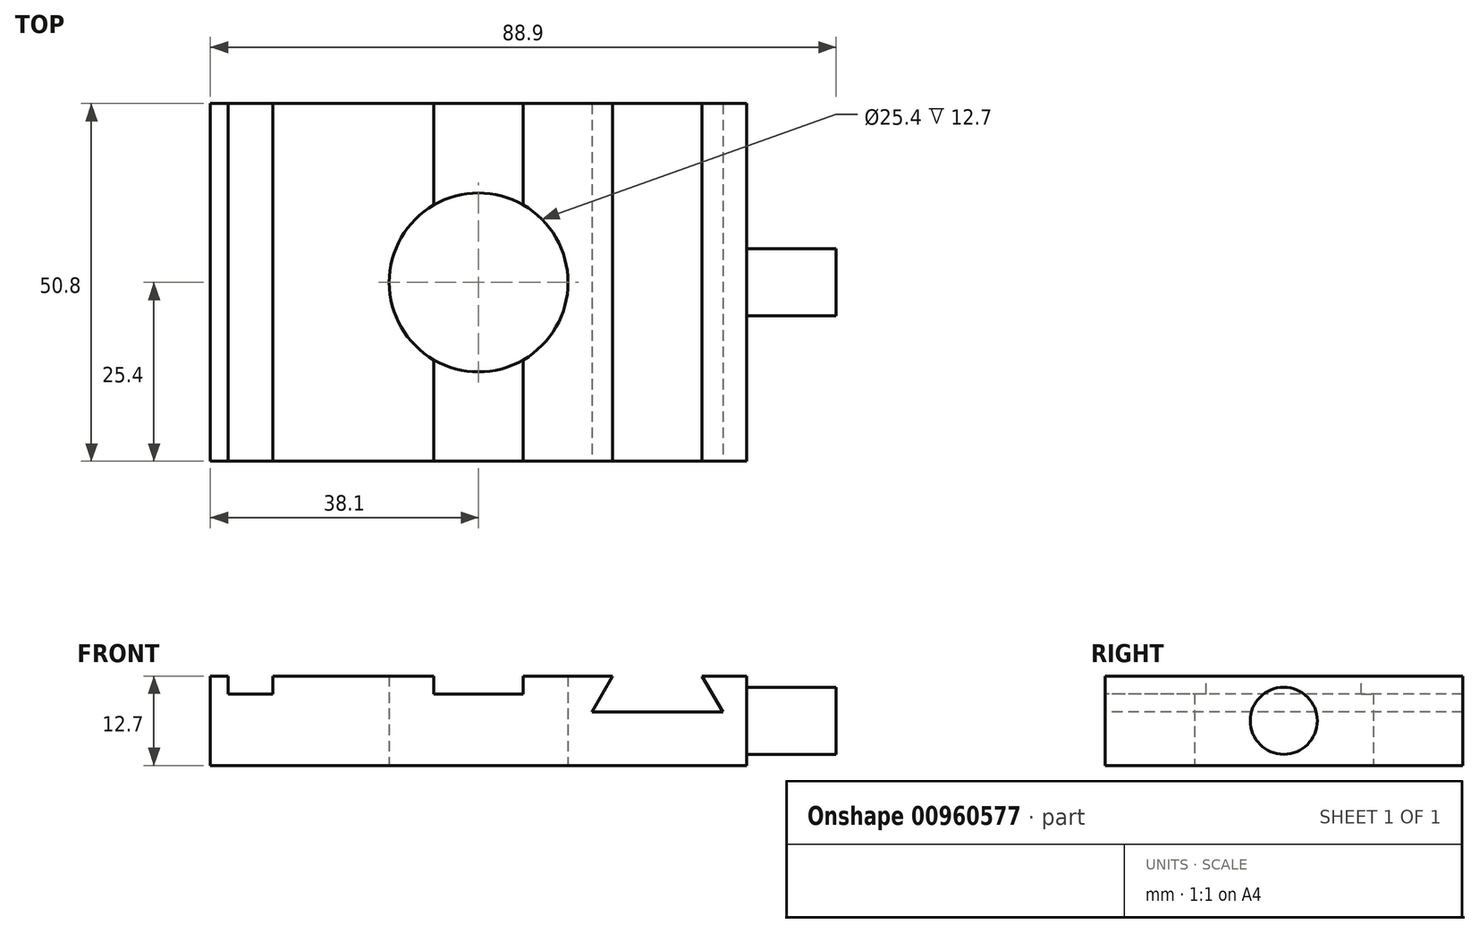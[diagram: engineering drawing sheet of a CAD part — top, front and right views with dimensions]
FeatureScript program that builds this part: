
annotation { "Feature Type Name" : "Feature", "Feature Type Description" : "" }
export const myFeature = defineFeature(function(context is Context, id is Id, definition is map)
    precondition{}
    {
        {
            var Q0;
            Q0=qCreatedBy(makeId("Top.planeOp"),FACE);
            var sketch = newSketch(context, id + "F0", { "sketchPlane" : qUnion([Q0])});
            skLineSegment(sketch, "E0.bottom", {"start": v(38.1, -25.4) * mm, "end": v(-38.1, -25.4) * mm});
            skLineSegment(sketch, "E0.top", {"start": v(38.1, 25.4) * mm, "end": v(-38.1, 25.4) * mm});
            skLineSegment(sketch, "E0.left", {"start": v(38.1, -25.4) * mm, "end": v(38.1, 25.4) * mm});
            skLineSegment(sketch, "E0.right", {"start": v(-38.1, -25.4) * mm, "end": v(-38.1, 25.4) * mm});
            skPoint(sketch, "E0.middle", {"position": v(0, 0) * mm});
            skCircle(sketch, "E1", {"center": v(0, 0) * mm, "radius": 12.7 * mm});
            skSolve(sketch);
        }
        {
            var Q0;
            Q0=makeQuery(id+"F0.imprint","IMPRINT",FACE,{"disambiguationData":[TD([[makeQuery(id+"F0.imprint","IMPRINT",EDGE,{"derivedFrom":sQuery(id+"F0.wireOp",EDGE,"E0.bottom")}),-1.0]])]});
            extrude(context, id + "F1", {"entities" : qUnion([Q0]), "depth" : 12.7 * mm, "offsetDistance" : 25.4 * mm});
        }
        {
            var Q0;
            Q0=makeQuery(id+"F1.opExtrude","CAP_FACE",FACE,{"disambiguationData":[OSD([sQuery(id+"F0.wireOp",EDGE,"E0.bottom"),sQuery(id+"F0.wireOp",EDGE,"E0.top"),sQuery(id+"F0.wireOp",EDGE,"E0.left"),sQuery(id+"F0.wireOp",EDGE,"E0.right"),sQuery(id+"F0.wireOp",EDGE,"E1")])],"isStart":false});
            var sketch = newSketch(context, id + "F2", { "sketchPlane" : qUnion([Q0])});
            skLineSegment(sketch, "E2.bottom", {"start": v(-35.56, 25.4) * mm, "end": v(-29.21, 25.4) * mm});
            skLineSegment(sketch, "E2.top", {"start": v(-35.56, -25.4) * mm, "end": v(-29.21, -25.4) * mm});
            skLineSegment(sketch, "E2.left", {"start": v(-35.56, 25.4) * mm, "end": v(-35.56, -25.4) * mm});
            skLineSegment(sketch, "E2.right", {"start": v(-29.21, 25.4) * mm, "end": v(-29.21, -25.4) * mm});
            skLineSegment(sketch, "E3", {"start": v(-6.35, 25.4) * mm, "end": v(-6.35, -25.4) * mm});
            skLineSegment(sketch, "E4", {"start": v(-6.35, -25.4) * mm, "end": v(6.35, -25.4) * mm});
            skLineSegment(sketch, "E5", {"start": v(6.35, -25.4) * mm, "end": v(6.35, 25.4) * mm});
            skPoint(sketch, "E6", {"position": v(0, 0) * mm});
            skLineSegment(sketch, "E7", {"start": v(-6.35, 25.4) * mm, "end": v(6.35, 25.4) * mm});
            skLineSegment(sketch, "E8", {"start": v(0, 25.4) * mm, "end": v(0, -25.4) * mm, "construction": true});
            skSolve(sketch);
        }
        {
            var Q0;
            Q0=makeQuery(id+"F2.imprint","IMPRINT",FACE,{"disambiguationData":[TD([[makeQuery(id+"F2.imprint","IMPRINT",EDGE,{"derivedFrom":sQuery(id+"F2.wireOp",EDGE,"E2.bottom")}),1.0]])]});
            var Q1;
            {var subQ0=sQuery(id+"F2.wireOp",EDGE,"E4");Q1=makeQuery(id+"F2.imprint","IMPRINT",FACE,{"disambiguationData":[TD([[makeQuery(id+"F2.imprint","IMPRINT",EDGE,{"derivedFrom":subQ0}),-1.0]])]});}
            var Q2;
            {var subQ0=sQuery(id+"F2.wireOp",EDGE,"E7");Q2=makeQuery(id+"F2.imprint","IMPRINT",FACE,{"disambiguationData":[TD([[makeQuery(id+"F2.imprint","IMPRINT",EDGE,{"derivedFrom":subQ0}),1.0]])]});}
            extrude(context, id + "F3", {"entities" : qUnion([Q0, Q1, Q2]), "operationType" : NewBodyOperationType.REMOVE, "oppositeDirection" : true, "depth" : 2.54 * mm, "offsetDistance" : 25.4 * mm});
        }
        {
            var Q0;
            Q0=makeQuery(id+"F1.opExtrude","SWEPT_FACE",FACE,{"disambiguationData":[OSD([sQuery(id+"F0.wireOp",EDGE,"E0.bottom")])]});
            var sketch = newSketch(context, id + "F4", { "sketchPlane" : qUnion([Q0])});
            skLineSegment(sketch, "E9", {"start": v(19.05, 12.7) * mm, "end": v(16.12, 7.62) * mm});
            skLineSegment(sketch, "E10", {"start": v(16.12, 7.62) * mm, "end": v(34.68, 7.62) * mm});
            skLineSegment(sketch, "E11", {"start": v(34.68, 7.62) * mm, "end": v(31.75, 12.7) * mm});
            skLineSegment(sketch, "E12", {"start": v(25.4, 7.62) * mm, "end": v(25.4, 12.7) * mm, "construction": true});
            skSolve(sketch);
        }
        {
            var Q0;
            {var subQ0=sQuery(id+"F4.wireOp",EDGE,"E9");Q0=makeQuery(id+"F4.imprint","IMPRINT",FACE,{"disambiguationData":[TD([[makeQuery(id+"F4.imprint","IMPRINT",EDGE,{"derivedFrom":subQ0}),1.0]])]});}
            extrude(context, id + "F5", {"entities" : qUnion([Q0]), "operationType" : NewBodyOperationType.REMOVE, "endBound" : BoundingType.THROUGH_ALL, "oppositeDirection" : true, "depth" : 25.4 * mm, "offsetDistance" : 25.4 * mm});
        }
        {
            var Q0;
            Q0=makeQuery(id+"F1.opExtrude","SWEPT_FACE",FACE,{"disambiguationData":[OSD([sQuery(id+"F0.wireOp",EDGE,"E0.left")])]});
            var sketch = newSketch(context, id + "F6", { "sketchPlane" : qUnion([Q0])});
            skCircle(sketch, "E13", {"center": v(0, 6.35) * mm, "radius": 4.76 * mm});
            skPoint(sketch, "E13.centerSnap0", {"position": v(-25.4, 6.35) * mm});
            skPoint(sketch, "E13.centerSnap1", {"position": v(0, 12.7) * mm});
            skSolve(sketch);
        }
        {
            var Q0;
            Q0=makeQuery(id+"F6.imprint","IMPRINT",FACE,{"disambiguationData":[TD([[makeQuery(id+"F6.imprint","IMPRINT",EDGE,{"derivedFrom":sQuery(id+"F6.wireOp",EDGE,"E13")}),1.0]])]});
            extrude(context, id + "F7", {"entities" : qUnion([Q0]), "operationType" : NewBodyOperationType.ADD, "depth" : 12.7 * mm, "offsetDistance" : 25.4 * mm});
        }
    });
